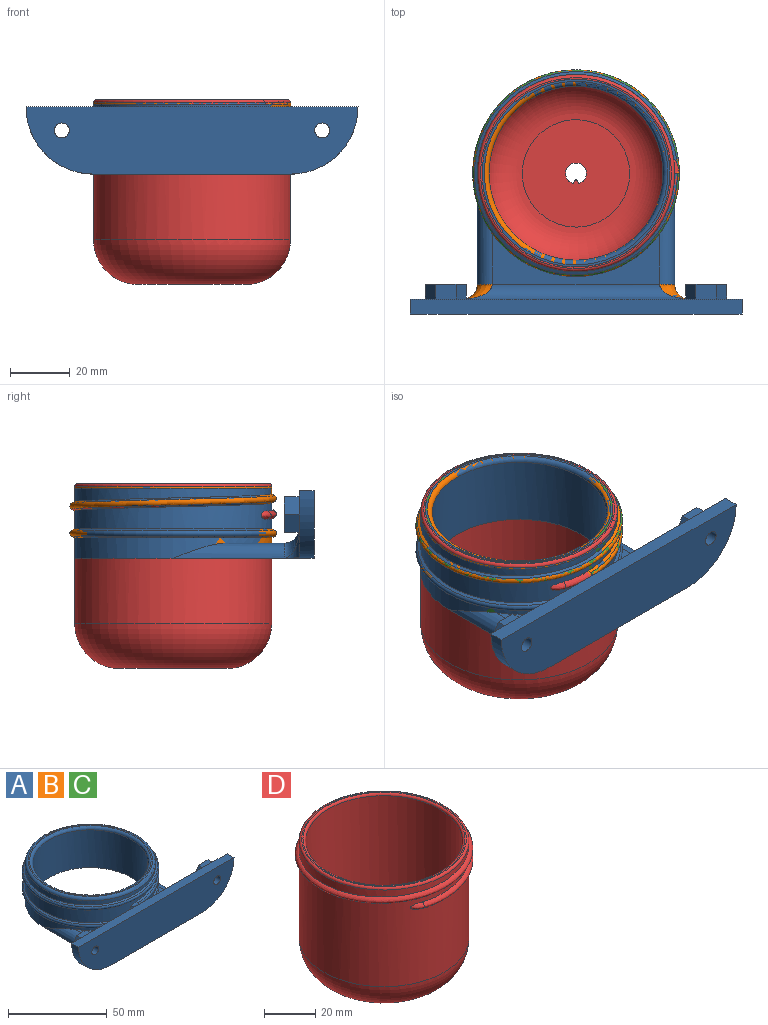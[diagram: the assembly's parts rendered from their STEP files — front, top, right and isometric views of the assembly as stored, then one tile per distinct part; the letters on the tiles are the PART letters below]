
ASSEMBLY  parts=4 mates=1
PART A: 60 faces, bbox 111.3x87.6x25 mm
  f0: plane 111.32x21.98mm, normal (0,1,0), area 1287.4mm2, adj f20,f21,f22,f23,f24,f25,f26,f27
  f1: plane 56.16x19.75mm, normal (0,0,1), area 490.8mm2, adj f3,f23,f56,f58
  f2: cylinder r=33.08mm len=66.16mm, axis (0,0,-1), area 2033mm2, adj f6,f8,f9,f10,f11,f12,f13,f16
  f3: cylinder r=33.08mm len=66.16mm, axis (0,0,-1), area 985.9mm2, adj f1,f14,f19,f56,f58
  f4: plane 62.96x62.96mm, normal (0,0,1), area 136.9mm2, adj f16,f17
  f5: cylinder r=29.18mm len=58.36mm, axis (0,0,-1), area 4290.2mm2, adj f17,f19
  f6: bspline ~78.58x68.05mm, area 282.3mm2, adj f2,f7,f9,f11
  f7: bspline ~80.69x69.88mm, area 663.5mm2, adj f6,f8,f9,f11
  f8: bspline ~78.58x68.05mm, area 282.3mm2, adj f2,f7,f9,f11
  f9: bspline ~4x3mm, area 11.5mm2, adj f2,f6,f7,f8,f10
  f10: plane 0.57x0.3mm, normal (0,1,0), area 0.1mm2, adj f2,f9
  f11: bspline ~4x3mm, area 11.5mm2, adj f2,f6,f7,f8,f12
  f12: plane 0.57x0.3mm, normal (-1,0,0), area 0.1mm2, adj f2,f11
  f13: cone r=33.08mm half-angle=62.2deg, axis (0,0,-1), area 225.8mm2, adj f2,f15
  f14: cone r=33.08mm half-angle=62.2deg, axis (0,0,1), area 225.8mm2, adj f3,f15
  f15: torus R=33.5mm, axis (0,0,-1), area 530.7mm2, adj f13,f14
  f16: torus R=31.48mm, axis (0,0,1), area 513.2mm2, adj f2,f4
  f17: torus R=30.78mm, axis (0,0,1), area 470mm2, adj f4,f5
  f18: plane 111.32x22.54mm, normal (0,-1,0), area 2251mm2, adj f19,f20,f21,f24,f40,f55
  f19: plane 80.32x66.16mm, normal (0,0,-1), area 2169.2mm2, adj f3,f5,f18,f21,f24,f56,f58
  f20: plane 111.32x5mm, normal (0,0,1), area 556.6mm2, adj f0,f18,f21,f24
  f21: cylinder r=22.58mm len=22.58mm, axis (0,-1,0), area 189.7mm2, adj f0,f18,f19,f20,f22
  f22: cylinder r=5mm len=10mm, axis (0,0,1), area 37.1mm2, adj f0,f21,f59
  f23: cylinder r=5mm len=76.16mm, axis (1,0,0), area 519.6mm2, adj f0,f1,f57,f59
  f24: cylinder r=22.58mm len=22.58mm, axis (0,-1,0), area 189.7mm2, adj f0,f18,f19,f20,f25
  f25: cylinder r=5mm len=10mm, axis (0,0,-1), area 37.1mm2, adj f0,f24,f57
  f26: plane 6.84x5mm, normal (0,0,-1), area 34.2mm2, adj f0,f27,f37,f38
  f27: plane 5.93x5mm, normal (-0.87,0,-0.5), area 34.2mm2, adj f0,f26,f28,f38
  f28: plane 5.93x5mm, normal (-0.87,0,0.5), area 34.2mm2, adj f0,f27,f29,f38
  f29: plane 6.84x5mm, normal (0,0,1), area 34.2mm2, adj f0,f28,f30,f38
  f30: plane 5.93x5mm, normal (0.87,0,0.5), area 34.2mm2, adj f0,f29,f37,f38
  f31: plane 5x3.93mm, normal (0.87,0,0.5), area 22.7mm2, adj f32,f36,f38,f39
  f32: plane 5x4.53mm, normal (0,0,1), area 22.7mm2, adj f31,f33,f38,f39
  f33: plane 5x3.93mm, normal (-0.87,0,0.5), area 22.7mm2, adj f32,f34,f38,f39
  f34: plane 5x3.93mm, normal (-0.87,0,-0.5), area 22.7mm2, adj f33,f35,f38,f39
  f35: plane 5x4.53mm, normal (0,0,-1), area 22.7mm2, adj f34,f36,f38,f39
  f36: plane 5x3.93mm, normal (0.87,0,-0.5), area 22.7mm2, adj f31,f35,f38,f39
  f37: plane 5.93x5mm, normal (0.87,0,-0.5), area 34.2mm2, adj f0,f26,f30,f38
  f38: plane 13.68x11.85mm, normal (0,1,0), area 68.2mm2, adj f26,f27,f28,f29,f30,f31,f32,f33
  f39: plane 9.06x7.85mm, normal (0,1,0), area 33.7mm2, adj f31,f32,f33,f34,f35,f36,f40
  f40: cylinder r=2.5mm len=5mm, axis (0,1,0), area 78.5mm2, adj f18,f39
  f41: plane 6.84x5mm, normal (0,0,-1), area 34.2mm2, adj f0,f42,f52,f53
  f42: plane 5.93x5mm, normal (-0.87,0,-0.5), area 34.2mm2, adj f0,f41,f43,f53
  f43: plane 5.93x5mm, normal (-0.87,0,0.5), area 34.2mm2, adj f0,f42,f44,f53
  f44: plane 6.84x5mm, normal (0,0,1), area 34.2mm2, adj f0,f43,f45,f53
  f45: plane 5.93x5mm, normal (0.87,0,0.5), area 34.2mm2, adj f0,f44,f52,f53
  f46: plane 5x3.93mm, normal (-0.87,0,0.5), area 22.7mm2, adj f47,f51,f53,f54
  f47: plane 5x3.93mm, normal (-0.87,0,-0.5), area 22.7mm2, adj f46,f48,f53,f54
  f48: plane 5x4.53mm, normal (0,0,-1), area 22.7mm2, adj f47,f49,f53,f54
  f49: plane 5x3.93mm, normal (0.87,0,-0.5), area 22.7mm2, adj f48,f50,f53,f54
  f50: plane 5x3.93mm, normal (0.87,0,0.5), area 22.7mm2, adj f49,f51,f53,f54
  f51: plane 5x4.53mm, normal (0,0,1), area 22.7mm2, adj f46,f50,f53,f54
  f52: plane 5.93x5mm, normal (0.87,0,-0.5), area 34.2mm2, adj f0,f41,f45,f53
  f53: plane 13.68x11.85mm, normal (0,1,0), area 68.2mm2, adj f41,f42,f43,f44,f45,f46,f47,f48
  f54: plane 9.06x7.85mm, normal (0,1,0), area 33.7mm2, adj f46,f47,f48,f49,f50,f51,f55
  f55: cylinder r=2.5mm len=5mm, axis (0,1,0), area 78.5mm2, adj f18,f54
  f56: cylinder r=5mm len=37.24mm, axis (0,-1,0), area 223.8mm2, adj f1,f3,f19,f57
  f57: bspline ~10x10mm, area 26.4mm2, adj f23,f25,f56
  f58: cylinder r=5mm len=37.24mm, axis (0,1,0), area 223.8mm2, adj f1,f3,f19,f59
  f59: bspline ~10x10mm, area 26.4mm2, adj f22,f23,f58
PART B: same geometry as A
PART C: same geometry as A
PART D: 19 faces, bbox 71.4x81.4x62 mm
  f0: cylinder r=33mm len=66mm, axis (0,0,1), area 807.2mm2, adj f1,f14,f15,f18
  f1: cylinder r=33mm len=66mm, axis (0,0,1), area 7952.6mm2, adj f0,f5,f14,f16
  f2: plane 36x36mm, normal (0,0,-1), area 981mm2, adj f5,f8,f9,f10,f11,f12,f13
  f3: plane 36x36mm, normal (0,0,1), area 981mm2, adj f7,f8,f9,f10,f11,f12,f13
  f4: plane 64x64mm, normal (0,0,1), area 99.7mm2, adj f17,f18
  f5: torus R=18mm, axis (0,0,-1), area 4078.5mm2, adj f1,f2
  f6: cylinder r=30.5mm len=61mm, axis (0,0,1), area 8815.3mm2, adj f7,f17
  f7: torus R=18mm, axis (0,0,-1), area 3202.4mm2, adj f3,f6
  f8: plane 2.5x0.74mm, normal (-0.87,0.5,0), area 2.1mm2, adj f2,f3,f11,f13
  f9: plane 2.5x0.74mm, normal (0.87,0.5,0), area 2.1mm2, adj f2,f3,f11,f12
  f10: cylinder r=3.5mm len=7mm, axis (0,0,-1), area 48.5mm2, adj f2,f3,f12,f13
  f11: cylinder r=0.4mm len=2.5mm, axis (0,0,-1), area 2.1mm2, adj f2,f3,f8,f9
  f12: cylinder r=0.4mm len=2.5mm, axis (0,0,-1), area 1.4mm2, adj f2,f3,f9,f10
  f13: cylinder r=0.4mm len=2.5mm, axis (0,0,-1), area 1.4mm2, adj f2,f3,f8,f10
  f14: bspline ~81.41x70.5mm, area 1215.2mm2, adj f0,f1,f15,f16
  f15: bspline ~5x4.13mm, area 17.2mm2, adj f0,f14
  f16: bspline ~4.64x3.91mm, area 17.8mm2, adj f1,f14
  f17: torus R=31.5mm, axis (0,0,1), area 304.6mm2, adj f4,f6
  f18: torus R=32mm, axis (0,0,1), area 322.1mm2, adj f0,f4
PLACE A at identity
PLACE B at identity fixed
PLACE C at identity
PLACE D t=(0,0,3)mm
MATE cylindrical D.f0 <-> B.f2  axis (0,0,1) through (0,0,19)mm
